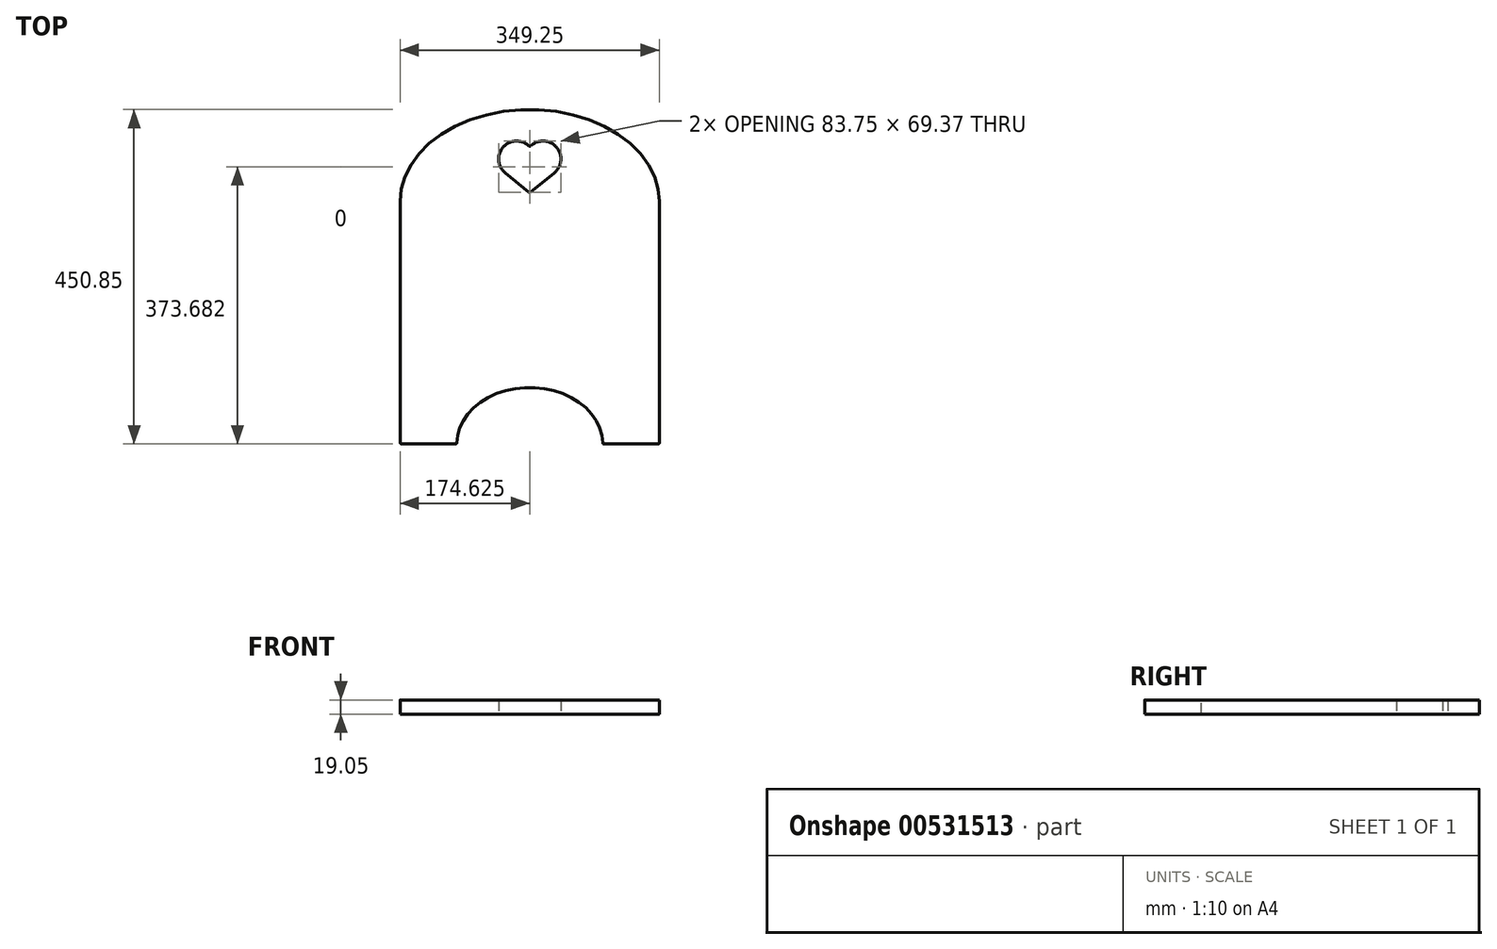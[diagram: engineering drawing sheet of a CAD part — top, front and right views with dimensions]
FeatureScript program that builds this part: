
annotation { "Feature Type Name" : "Feature", "Feature Type Description" : "" }
export const myFeature = defineFeature(function(context is Context, id is Id, definition is map)
    precondition{}
    {
        {
            var Q0;
            Q0=qCreatedBy(makeId("Top.planeOp"),FACE);
            var sketch = newSketch(context, id + "F0", { "sketchPlane" : qUnion([Q0])});
            skLineSegment(sketch, "E0.bottom", {"start": v(1.59, 0) * mm, "end": v(74.63, 0) * mm});
            skLineSegment(sketch, "E0.left", {"start": v(0, 1.59) * mm, "end": v(0, 327.02) * mm});
            skLineSegment(sketch, "E0.right", {"start": v(349.25, 1.59) * mm, "end": v(349.25, 327.02) * mm});
            skLineSegment(sketch, "E1", {"start": v(174.63, 0) * mm, "end": v(174.63, 450.85) * mm, "construction": true});
            skLineSegment(sketch, "E2", {"start": v(174.62, 152.4) * mm, "end": v(0, 327.02) * mm, "construction": true});
            skLineSegment(sketch, "E3", {"start": v(0, 327.02) * mm, "end": v(349.25, 327.02) * mm, "construction": true});
            skLineSegment(sketch, "E4", {"start": v(349.25, 327.02) * mm, "end": v(174.63, 152.4) * mm, "construction": true});
            skLineSegment(sketch, "E5", {"start": v(174.63, 76.2) * mm, "end": v(76.2, 76.2) * mm, "construction": true});
            skLineSegment(sketch, "E6", {"start": v(76.2, 76.2) * mm, "end": v(76.2, 0) * mm, "construction": true});
            skLineSegment(sketch, "E7.trimOffspring", {"start": v(274.62, 0) * mm, "end": v(347.66, 0) * mm});
            skLineSegment(sketch, "E8.0", {"start": v(318.3, 296.08) * mm, "end": v(174.63, 439.77) * mm, "construction": true});
            skLineSegment(sketch, "E8.1", {"start": v(174.63, 439.77) * mm, "end": v(30.94, 296.08) * mm, "construction": true});
            skEllipticalArc(sketch, "E9", {});
            skPoint(sketch, "E10.orphan", {"position": v(349.25, 447.67) * mm});
            skPoint(sketch, "E11.orphan", {"position": v(0, 454.02) * mm});
            skLineSegment(sketch, "E12", {"start": v(173.62, 339.35) * mm, "end": v(141.63, 365.33) * mm});
            skLineSegment(sketch, "E13", {"start": v(207.62, 365.33) * mm, "end": v(175.63, 339.35) * mm});
            skLineSegment(sketch, "E14", {"start": v(130.18, 374.63) * mm, "end": v(174.63, 374.63) * mm, "construction": true});
            skLineSegment(sketch, "E15", {"start": v(174.63, 374.63) * mm, "end": v(219.08, 374.63) * mm, "construction": true});
            skLineSegment(sketch, "E16", {"start": v(156.9, 384.15) * mm, "end": v(174.63, 384.15) * mm, "construction": true});
            skLineSegment(sketch, "E17", {"start": v(174.63, 384.15) * mm, "end": v(192.35, 384.15) * mm, "construction": true});
            skArc(sketch, "E18", {"start": v(207.62, 365.33) * mm, "mid": v(210.59, 400.12) * mm, "end": v(175.71, 401.79) * mm});
            skArc(sketch, "E19", {"start": v(173.54, 401.79) * mm, "mid": v(138.66, 400.12) * mm, "end": v(141.63, 365.33) * mm});
            skLineSegment(sketch, "E20", {"start": v(174.63, 450.85) * mm, "end": v(43.85, 450.85) * mm, "construction": true});
            skLineSegment(sketch, "E21", {"start": v(156.9, 408.4) * mm, "end": v(100.91, 408.4) * mm, "construction": true});
            skLineSegment(sketch, "E22", {"start": v(100.91, 408.4) * mm, "end": v(100.91, 450.85) * mm, "construction": true});
            skLineSegment(sketch, "E23", {"start": v(174.63, 338.54) * mm, "end": v(30.94, 338.54) * mm, "construction": true});
            skLineSegment(sketch, "E24", {"start": v(30.94, 338.54) * mm, "end": v(30.94, 296.08) * mm, "construction": true});
            skPoint(sketch, "E25.visualSharp", {"position": v(174.63, 338.54) * mm});
            skArc(sketch, "E25.filletArc", {"start": v(173.62, 339.35) * mm, "mid": v(174.63, 339) * mm, "end": v(175.63, 339.35) * mm});
            skPoint(sketch, "E26.visualSharp", {"position": v(174.62, 400.7) * mm});
            skArc(sketch, "E26.filletArc", {"start": v(173.54, 401.79) * mm, "mid": v(174.62, 401.35) * mm, "end": v(175.71, 401.79) * mm});
            skEllipticalArc(sketch, "E27", {});
            skPoint(sketch, "E28.visualSharp", {"position": v(0, 0) * mm});
            skArc(sketch, "E28.filletArc", {"start": v(0, 1.59) * mm, "mid": v(0.46, 0.46) * mm, "end": v(1.59, 0) * mm});
            skPoint(sketch, "E29.visualSharp", {"position": v(76.2, 0) * mm});
            skArc(sketch, "E29.filletArc", {"start": v(74.63, 0) * mm, "mid": v(75.74, 0.45) * mm, "end": v(76.22, 1.55) * mm});
            skPoint(sketch, "E30.visualSharp", {"position": v(273.05, 0) * mm});
            skArc(sketch, "E30.filletArc", {"start": v(273.03, 1.55) * mm, "mid": v(273.5, 0.45) * mm, "end": v(274.62, 0) * mm});
            skPoint(sketch, "E31.visualSharp", {"position": v(349.25, 0) * mm});
            skArc(sketch, "E31.filletArc", {"start": v(347.66, 0) * mm, "mid": v(348.79, 0.46) * mm, "end": v(349.25, 1.59) * mm});
            const initialGuessF0  = {"E9": [0.174625, 0.327025, 0, 1, 0.123825, 0.174625, 4.71238898038469, 1.5707963267948966], "E27": [0.174625, 0, 0, 1, 0.0762, 0.098425, 4.732677850315133, 1.5505074568644543]};
            skSetInitialGuess(sketch, initialGuessF0);
            skSolve(sketch);
        }
        {
            var Q0;
            Q0 = qSketchRegion(id + "F0", true);
            extrude(context, id + "F1", {"entities" : qUnion([Q0]), "depth" : 19.05 * mm, "offsetDistance" : 25.4 * mm});
        }
    });
